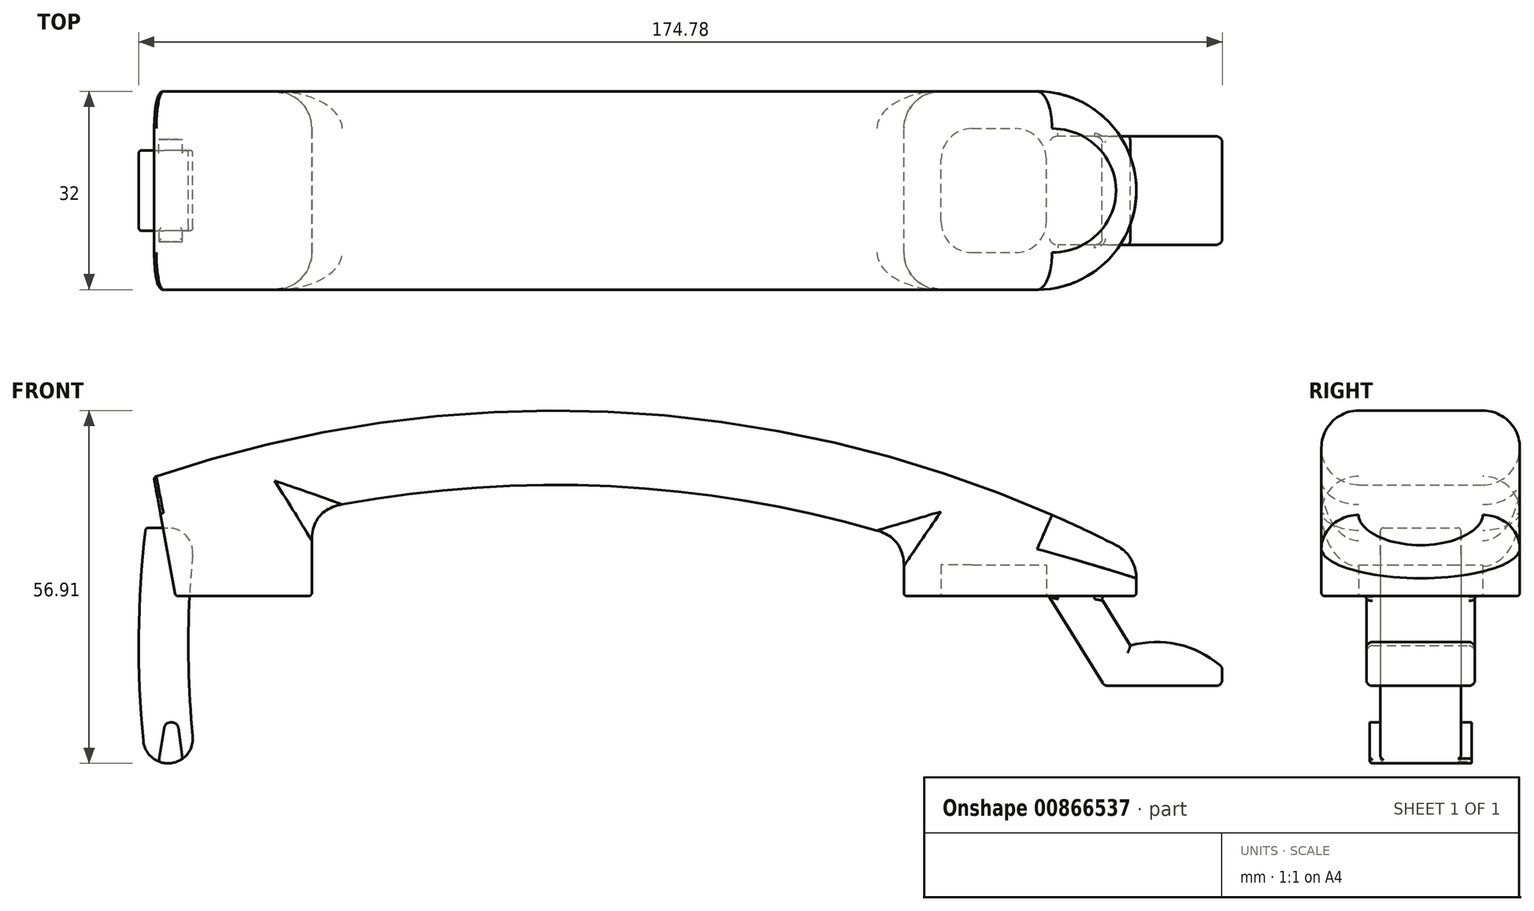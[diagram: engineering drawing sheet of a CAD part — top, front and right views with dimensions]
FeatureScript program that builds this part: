
annotation { "Feature Type Name" : "Feature", "Feature Type Description" : "" }
export const myFeature = defineFeature(function(context is Context, id is Id, definition is map)
    precondition{}
    {
        {
            var Q0;
            Q0=qCreatedBy(makeId("Front.planeOp"),FACE);
            var sketch = newSketch(context, id + "F0", { "sketchPlane" : qUnion([Q0])});
            skLineSegment(sketch, "E0", {"start": v(0, 0) * mm, "end": v(155, 0) * mm, "construction": true});
            skLineSegment(sketch, "E1", {"start": v(155, 0) * mm, "end": v(155, 6.5) * mm});
            skLineSegment(sketch, "E2", {"start": v(0, 0) * mm, "end": v(-3.5, 0) * mm});
            skLineSegment(sketch, "E3", {"start": v(0, 0) * mm, "end": v(-3.5, 19.18) * mm});
            skArc(sketch, "E4", {"start": v(155, 6.5) * mm, "mid": v(77.06, 29.27) * mm, "end": v(-3.5, 19.18) * mm});
            skLineSegment(sketch, "E5", {"start": v(155, 0) * mm, "end": v(117.5, 0) * mm});
            skLineSegment(sketch, "E6", {"start": v(117.5, 0) * mm, "end": v(117.5, 9.25) * mm});
            skArc(sketch, "E7.trimOffspring", {"start": v(117.5, 9.25) * mm, "mid": v(70.04, 17.7) * mm, "end": v(22, 13.8) * mm});
            skLineSegment(sketch, "E8", {"start": v(0, 0) * mm, "end": v(22, 0) * mm});
            skLineSegment(sketch, "E9", {"start": v(22, 0) * mm, "end": v(22, 13.8) * mm});
            skSolve(sketch);
        }
        {
            var Q0;
            Q0 = qSketchRegion(id + "F0", true);
            extrude(context, id + "F1", {"entities" : qUnion([Q0]), "endBound" : BoundingType.SYMMETRIC, "depth" : 32 * mm, "offsetDistance" : 25 * mm});
        }
        {
            var Q0;
            Q0=makeQuery(id+"F1.opExtrude","CAP_EDGE",EDGE,{"disambiguationData":[OSD([sQuery(id+"F0.wireOp",EDGE,"E1")])],"isStart":true});
            var Q1;
            Q1=makeQuery(id+"F1.opExtrude","CAP_EDGE",EDGE,{"disambiguationData":[OSD([sQuery(id+"F0.wireOp",EDGE,"E1")])],"isStart":false});
            fillet(context, id + "F2", {"entities" : qUnion([Q0, Q1]), "radius" : 16 * mm, "tangentPropagation" : true, "allowEdgeOverflow" : false});
        }
        {
            var Q0;
            Q0=makeQuery(id+"F1.opExtrude","CAP_EDGE",EDGE,{"disambiguationData":[OSD([sQuery(id+"F0.wireOp",EDGE,"E4")])],"isStart":false});
            var Q1;
            Q1=makeQuery(id+"F1.opExtrude","CAP_EDGE",EDGE,{"disambiguationData":[OSD([sQuery(id+"F0.wireOp",EDGE,"E7.trimOffspring")])],"isStart":false});
            var Q2;
            Q2=makeQuery(id+"F1.opExtrude","CAP_EDGE",EDGE,{"disambiguationData":[OSD([sQuery(id+"F0.wireOp",EDGE,"E7.trimOffspring")])],"isStart":true});
            var Q3;
            Q3=makeQuery(id+"F1.opExtrude","CAP_EDGE",EDGE,{"disambiguationData":[OSD([sQuery(id+"F0.wireOp",EDGE,"E6")])],"isStart":true});
            var Q4;
            Q4=makeQuery(id+"F1.opExtrude","CAP_EDGE",EDGE,{"disambiguationData":[OSD([sQuery(id+"F0.wireOp",EDGE,"E6")])],"isStart":false});
            var Q5;
            Q5=makeQuery(id+"F1.opExtrude","CAP_EDGE",EDGE,{"disambiguationData":[OSD([sQuery(id+"F0.wireOp",EDGE,"E9")])],"isStart":false});
            var Q6;
            Q6=makeQuery(id+"F1.opExtrude","CAP_EDGE",EDGE,{"disambiguationData":[OSD([sQuery(id+"F0.wireOp",EDGE,"E4")])],"isStart":true});
            var Q7;
            Q7=makeQuery(id+"F1.opExtrude","CAP_EDGE",EDGE,{"disambiguationData":[OSD([sQuery(id+"F0.wireOp",EDGE,"E9")])],"isStart":true});
            fillet(context, id + "F3", {"entities" : qUnion([Q0, Q1, Q2, Q3, Q4, Q5, Q6, Q7]), "radius" : 6 * mm, "tangentPropagation" : true, "allowEdgeOverflow" : false});
        }
        {
            var Q0;
            Q0=makeQuery(id+"F3.opFillet","BLEND_EDGE",EDGE,{"blendedFrom":[makeQuery(id+"F1.opExtrude","CAP_EDGE",EDGE,{"disambiguationData":[OSD([sQuery(id+"F0.wireOp",EDGE,"E6")])],"isStart":false}),makeQuery(id+"F1.opExtrude","CAP_EDGE",EDGE,{"disambiguationData":[OSD([sQuery(id+"F0.wireOp",EDGE,"E7.trimOffspring")])],"isStart":false})],"blendedInto":[]});
            var Q1;
            Q1=makeQuery(id+"F3.opFillet","BLEND_EDGE",EDGE,{"blendedFrom":[makeQuery(id+"F1.opExtrude","CAP_EDGE",EDGE,{"disambiguationData":[OSD([sQuery(id+"F0.wireOp",EDGE,"E7.trimOffspring")])],"isStart":false}),makeQuery(id+"F1.opExtrude","CAP_EDGE",EDGE,{"disambiguationData":[OSD([sQuery(id+"F0.wireOp",EDGE,"E9")])],"isStart":false})],"blendedInto":[]});
            var Q2;
            {var subQ0=sQuery(id+"F0.wireOp",EDGE,"E1");Q2=makeQuery(id+"F3.opFillet","BLEND_EDGE",EDGE,{"blendedFrom":[makeQuery(id+"F2.opFillet","BLEND_EDGE",EDGE,{"blendedFrom":[makeQuery(id+"F1.opExtrude","CAP_EDGE",EDGE,{"disambiguationData":[OSD([subQ0])],"isStart":false}),makeQuery(id+"F1.opExtrude","SWEPT_FACE",FACE,{"disambiguationData":[OSD([sQuery(id+"F0.wireOp",EDGE,"E4")])]})],"blendedInto":[makeQuery(id+"F1.opExtrude","SWEPT_FACE",FACE,{"disambiguationData":[OSD([sQuery(id+"F0.wireOp",EDGE,"E4")])]})]}),makeQuery(id+"F2.opFillet","BLEND_FACE",FACE,{"disambiguationData":[OSD([subQ0])]})],"blendedInto":[makeQuery(id+"F2.opFillet","BLEND_FACE",FACE,{"disambiguationData":[OSD([subQ0])]})]});}
            var Q3;
            {var subQ0=makeQuery(id+"F1.opExtrude","SWEPT_FACE",FACE,{"disambiguationData":[OSD([sQuery(id+"F0.wireOp",EDGE,"E4")])]});Q3=makeQuery(id+"F3.opFillet","BLEND_EDGE",EDGE,{"blendedFrom":[makeQuery(id+"F2.opFillet","BLEND_EDGE",EDGE,{"blendedFrom":[makeQuery(id+"F1.opExtrude","CAP_EDGE",EDGE,{"disambiguationData":[OSD([sQuery(id+"F0.wireOp",EDGE,"E1")])],"isStart":false}),subQ0],"blendedInto":[subQ0]}),subQ0],"blendedInto":[subQ0]});}
            var Q4;
            {var subQ0=sQuery(id+"F0.wireOp",EDGE,"E4");Q4=makeQuery(id+"F3.opFillet","BLEND_EDGE",EDGE,{"blendedFrom":[makeQuery(id+"F2.opFillet","BLEND_EDGE",EDGE,{"blendedFrom":[makeQuery(id+"F1.opExtrude","CAP_EDGE",EDGE,{"disambiguationData":[OSD([sQuery(id+"F0.wireOp",EDGE,"E1")])],"isStart":false}),makeQuery(id+"F1.opExtrude","SWEPT_FACE",FACE,{"disambiguationData":[OSD([subQ0])]})],"blendedInto":[makeQuery(id+"F1.opExtrude","SWEPT_FACE",FACE,{"disambiguationData":[OSD([subQ0])]})]}),makeQuery(id+"F1.opExtrude","CAP_EDGE",EDGE,{"disambiguationData":[OSD([subQ0])],"isStart":false})],"blendedInto":[]});}
            var Q5;
            Q5=makeQuery(id+"F3.opFillet","BLEND_EDGE",EDGE,{"blendedFrom":[makeQuery(id+"F1.opExtrude","CAP_EDGE",EDGE,{"disambiguationData":[OSD([sQuery(id+"F0.wireOp",EDGE,"E7.trimOffspring")])],"isStart":true}),makeQuery(id+"F1.opExtrude","CAP_EDGE",EDGE,{"disambiguationData":[OSD([sQuery(id+"F0.wireOp",EDGE,"E9")])],"isStart":true})],"blendedInto":[]});
            var Q6;
            Q6=makeQuery(id+"F3.opFillet","BLEND_EDGE",EDGE,{"blendedFrom":[makeQuery(id+"F1.opExtrude","CAP_EDGE",EDGE,{"disambiguationData":[OSD([sQuery(id+"F0.wireOp",EDGE,"E6")])],"isStart":true}),makeQuery(id+"F1.opExtrude","CAP_EDGE",EDGE,{"disambiguationData":[OSD([sQuery(id+"F0.wireOp",EDGE,"E7.trimOffspring")])],"isStart":true})],"blendedInto":[]});
            var Q7;
            Q7=makeQuery(id+"F1.opExtrude","SWEPT_EDGE",EDGE,{"disambiguationData":[OSD([sQuery(id+"F0.wireOp",EDGE,"E6"),sQuery(id+"F0.wireOp",EDGE,"E7.trimOffspring")])]});
            var Q8;
            Q8=makeQuery(id+"F1.opExtrude","SWEPT_EDGE",EDGE,{"disambiguationData":[OSD([sQuery(id+"F0.wireOp",EDGE,"E7.trimOffspring"),sQuery(id+"F0.wireOp",EDGE,"E9")])]});
            fillet(context, id + "F4", {"entities" : qUnion([Q0, Q1, Q2, Q3, Q4, Q5, Q6, Q7, Q8]), "radius" : 6 * mm, "rho" : 0.5, "crossSection" : FilletCrossSection.CONIC, "allowEdgeOverflow" : false});
        }
        {
            var Q0;
            Q0=qCreatedBy(makeId("Front.planeOp"),FACE);
            var sketch = newSketch(context, id + "F5", { "sketchPlane" : qUnion([Q0])});
            skLineSegment(sketch, "E10", {"start": v(149.36, 0) * mm, "end": v(140.86, 0) * mm});
            skLineSegment(sketch, "E11", {"start": v(149.86, -14.5) * mm, "end": v(140.86, 0) * mm});
            skLineSegment(sketch, "E12.0", {"start": v(154.06, -8) * mm, "end": v(149.1, 0) * mm});
            skLineSegment(sketch, "E13", {"start": v(149.86, -14.5) * mm, "end": v(168.86, -14.5) * mm});
            skLineSegment(sketch, "E14", {"start": v(168.86, -14.5) * mm, "end": v(168.86, -11.5) * mm});
            skArc(sketch, "E15", {"start": v(168.86, -11.5) * mm, "mid": v(161.9, -7.85) * mm, "end": v(154.06, -8) * mm});
            skPoint(sketch, "E16.start.orphan", {"position": v(157.1, 0) * mm});
            skLineSegment(sketch, "E17", {"start": v(155.1, 0) * mm, "end": v(149.1, 0) * mm});
            skSolve(sketch);
        }
        {
            var Q0;
            {var subQ1=sQuery(id+"F5.wireOp",EDGE,"E11");Q0=makeQuery(id+"F5.imprint","IMPRINT",FACE,{"disambiguationData":[TD([[makeQuery(id+"F5.imprint","IMPRINT",EDGE,{"derivedFrom":subQ1}),-1.0]])]});}
            extrude(context, id + "F6", {"entities" : qUnion([Q0]), "operationType" : NewBodyOperationType.ADD, "endBound" : BoundingType.SYMMETRIC, "depth" : 17.5 * mm, "offsetDistance" : 25 * mm});
        }
        {
            var Q0;
            Q0=makeQuery(id+"F6.opExtrude","CAP_EDGE",EDGE,{"disambiguationData":[OSD([sQuery(id+"F5.wireOp",EDGE,"E12.0")])],"isStart":false});
            var Q1;
            Q1=makeQuery(id+"F6.opExtrude","CAP_EDGE",EDGE,{"disambiguationData":[OSD([sQuery(id+"F5.wireOp",EDGE,"E15")])],"isStart":false});
            var Q2;
            Q2=makeQuery(id+"F6.opExtrude","CAP_EDGE",EDGE,{"disambiguationData":[OSD([sQuery(id+"F5.wireOp",EDGE,"E15")])],"isStart":true});
            var Q3;
            Q3=makeQuery(id+"F6.opExtrude","CAP_EDGE",EDGE,{"disambiguationData":[OSD([sQuery(id+"F5.wireOp",EDGE,"E12.0")])],"isStart":true});
            var Q4;
            Q4=makeQuery(id+"F6.opExtrude","SWEPT_EDGE",EDGE,{"disambiguationData":[OSD([sQuery(id+"F5.wireOp",EDGE,"E14"),sQuery(id+"F5.wireOp",EDGE,"E15")])]});
            var Q5;
            Q5=makeQuery(id+"F6.opExtrude","CAP_EDGE",EDGE,{"disambiguationData":[OSD([sQuery(id+"F5.wireOp",EDGE,"E11")])],"isStart":false});
            var Q6;
            Q6=makeQuery(id+"F6.opExtrude","CAP_EDGE",EDGE,{"disambiguationData":[OSD([sQuery(id+"F5.wireOp",EDGE,"E13")])],"isStart":false});
            var Q7;
            Q7=makeQuery(id+"F6.opExtrude","SWEPT_EDGE",EDGE,{"disambiguationData":[OSD([sQuery(id+"F5.wireOp",EDGE,"E11"),sQuery(id+"F5.wireOp",EDGE,"E13")])]});
            var Q8;
            Q8=makeQuery(id+"F6.opExtrude","CAP_EDGE",EDGE,{"disambiguationData":[OSD([sQuery(id+"F5.wireOp",EDGE,"E11")])],"isStart":true});
            var Q9;
            Q9=makeQuery(id+"F6.opExtrude","CAP_EDGE",EDGE,{"disambiguationData":[OSD([sQuery(id+"F5.wireOp",EDGE,"E13")])],"isStart":true});
            var Q10;
            Q10=makeQuery(id+"F6.opExtrude","SWEPT_FACE",FACE,{"disambiguationData":[OSD([sQuery(id+"F5.wireOp",EDGE,"E14")])]});
            fillet(context, id + "F7", {"entities" : qUnion([Q0, Q1, Q2, Q3, Q4, Q5, Q6, Q7, Q8, Q9, Q10]), "radius" : 1 * mm, "tangentPropagation" : true, "allowEdgeOverflow" : false});
        }
        {
            var Q0;
            Q0=qCreatedBy(makeId("Front.planeOp"),FACE);
            var sketch = newSketch(context, id + "F8", { "sketchPlane" : qUnion([Q0])});
            skArc(sketch, "E18", {"start": v(-4.8, 11) * mm, "mid": v(-5.92, -8) * mm, "end": v(-4.79, -27) * mm});
            skArc(sketch, "E19.0", {"start": v(3.26, 11) * mm, "mid": v(2.08, -8) * mm, "end": v(3.27, -27) * mm});
            skLineSegment(sketch, "E20", {"start": v(0, -27) * mm, "end": v(3.27, -27) * mm});
            skLineSegment(sketch, "E21", {"start": v(3.27, -27) * mm, "end": v(-4.79, -27) * mm});
            skLineSegment(sketch, "E22", {"start": v(0, 11) * mm, "end": v(-4.8, 11) * mm});
            skLineSegment(sketch, "E23", {"start": v(0, 11) * mm, "end": v(3.26, 11) * mm});
            skSolve(sketch);
        }
        {
            var Q0;
            {var subQ1=sQuery(id+"F8.wireOp",EDGE,"E18");Q0=makeQuery(id+"F8.imprint","IMPRINT",FACE,{"disambiguationData":[TD([[makeQuery(id+"F8.imprint","IMPRINT",EDGE,{"derivedFrom":subQ1}),1.0]])]});}
            extrude(context, id + "F9", {"entities" : qUnion([Q0]), "endBound" : BoundingType.SYMMETRIC, "depth" : 13 * mm, "offsetDistance" : 25 * mm});
        }
        {
            var Q0;
            Q0=qCreatedBy(makeId("Front.planeOp"),FACE);
            var sketch = newSketch(context, id + "F10", { "sketchPlane" : qUnion([Q0])});
            skLineSegment(sketch, "E24", {"start": v(-0.76, -27) * mm, "end": v(1.24, -27) * mm});
            skLineSegment(sketch, "E25", {"start": v(-0.76, -27) * mm, "end": v(-2.76, -27) * mm});
            skLineSegment(sketch, "E26", {"start": v(-0.66, -20.4) * mm, "end": v(-0.53, -20.4) * mm});
            skLineSegment(sketch, "E27", {"start": v(-0.66, -20.4) * mm, "end": v(-0.81, -20.4) * mm});
            skLineSegment(sketch, "E28", {"start": v(-1.8, -21.24) * mm, "end": v(-2.76, -27) * mm});
            skLineSegment(sketch, "E29", {"start": v(0.46, -21.27) * mm, "end": v(1.24, -27) * mm});
            skPoint(sketch, "E30.visualSharp", {"position": v(-1.66, -20.4) * mm});
            skArc(sketch, "E30.filletArc", {"start": v(-0.81, -20.4) * mm, "mid": v(-1.46, -20.64) * mm, "end": v(-1.8, -21.24) * mm});
            skPoint(sketch, "E31.visualSharp", {"position": v(0.34, -20.4) * mm});
            skArc(sketch, "E31.filletArc", {"start": v(0.46, -21.27) * mm, "mid": v(0.13, -20.65) * mm, "end": v(-0.53, -20.4) * mm});
            skSolve(sketch);
        }
        {
            var Q0;
            Q0 = qSketchRegion(id + "F10", true);
            var Q1;
            Q1 = qConstructionFilter(qBodyType(qCreatedBy(id + "F10" ,EDGE), BodyType.WIRE), ConstructionObject.NO);
            extrude(context, id + "F11", {"entities" : qUnion([Q0]), "operationType" : NewBodyOperationType.ADD, "surfaceEntities" : qUnion([Q1]), "endBound" : BoundingType.SYMMETRIC, "depth" : 16.5 * mm, "offsetDistance" : 25 * mm});
        }
        {
            var Q0;
            Q0=makeQuery(id+"F9.opExtrude","SWEPT_EDGE",EDGE,{"disambiguationData":[OSD([sQuery(id+"F8.wireOp",EDGE,"E18"),sQuery(id+"F8.wireOp",EDGE,"E21")])]});
            var Q1;
            Q1=makeQuery(id+"F9.opExtrude","SWEPT_EDGE",EDGE,{"disambiguationData":[OSD([sQuery(id+"F8.wireOp",EDGE,"E19.0"),sQuery(id+"F8.wireOp",EDGE,"E21")])]});
            fillet(context, id + "F12", {"entities" : qUnion([Q0, Q1]), "radius" : 4 * mm, "tangentPropagation" : true, "allowEdgeOverflow" : false});
        }
        {
            var Q0;
            Q0=makeQuery(id+"F1.opExtrude","SWEPT_EDGE",EDGE,{"disambiguationData":[OSD([sQuery(id+"F0.wireOp",EDGE,"E3"),sQuery(id+"F0.wireOp",EDGE,"E4")])]});
            var Q1;
            Q1=makeQuery(id+"F1.opExtrude","CAP_EDGE",EDGE,{"disambiguationData":[OSD([sQuery(id+"F0.wireOp",EDGE,"E8")])],"isStart":true});
            var Q2;
            Q2=makeQuery(id+"F1.opExtrude","SWEPT_EDGE",EDGE,{"disambiguationData":[OSD([sQuery(id+"F0.wireOp",EDGE,"E3"),sQuery(id+"F0.wireOp",EDGE,"E8")])]});
            var Q3;
            Q3=makeQuery(id+"F12.opFillet","BLEND_EDGE",EDGE,{"blendedFrom":[makeQuery(id+"F9.opExtrude","SWEPT_EDGE",EDGE,{"disambiguationData":[OSD([sQuery(id+"F8.wireOp",EDGE,"E18"),sQuery(id+"F8.wireOp",EDGE,"E21")])]}),makeQuery(id+"F11.opExtrude","CAP_FACE",FACE,{"disambiguationData":[OSD([sQuery(id+"F10.wireOp",EDGE,"E24"),sQuery(id+"F10.wireOp",EDGE,"E25"),sQuery(id+"F10.wireOp",EDGE,"E26"),sQuery(id+"F10.wireOp",EDGE,"E27"),sQuery(id+"F10.wireOp",EDGE,"E28"),sQuery(id+"F10.wireOp",EDGE,"E29"),sQuery(id+"F10.wireOp",EDGE,"E30.filletArc"),sQuery(id+"F10.wireOp",EDGE,"E31.filletArc")])],"isStart":false})],"blendedInto":[makeQuery(id+"F11.opExtrude","CAP_FACE",FACE,{"disambiguationData":[OSD([sQuery(id+"F10.wireOp",EDGE,"E24"),sQuery(id+"F10.wireOp",EDGE,"E25"),sQuery(id+"F10.wireOp",EDGE,"E26"),sQuery(id+"F10.wireOp",EDGE,"E27"),sQuery(id+"F10.wireOp",EDGE,"E28"),sQuery(id+"F10.wireOp",EDGE,"E29"),sQuery(id+"F10.wireOp",EDGE,"E30.filletArc"),sQuery(id+"F10.wireOp",EDGE,"E31.filletArc")])],"isStart":false})]});
            var Q4;
            {var subQ0=sQuery(id+"F8.wireOp",EDGE,"E21");var subQ1=sQuery(id+"F8.wireOp",EDGE,"E18");Q4=makeQuery(id+"F12.opFillet","BLEND_EDGE",EDGE,{"blendedFrom":[makeQuery(id+"F9.opExtrude","SWEPT_EDGE",EDGE,{"disambiguationData":[OSD([subQ1,subQ0])]}),makeQuery(id+"F9.opExtrude","CAP_FACE",FACE,{"disambiguationData":[OSD([subQ1,sQuery(id+"F8.wireOp",EDGE,"E19.0"),subQ0,sQuery(id+"F8.wireOp",EDGE,"E22"),sQuery(id+"F8.wireOp",EDGE,"E23")])],"isStart":false})],"blendedInto":[makeQuery(id+"F9.opExtrude","CAP_FACE",FACE,{"disambiguationData":[OSD([subQ1,sQuery(id+"F8.wireOp",EDGE,"E19.0"),subQ0,sQuery(id+"F8.wireOp",EDGE,"E22"),sQuery(id+"F8.wireOp",EDGE,"E23")])],"isStart":false})]});}
            var Q5;
            {var subQ0=sQuery(id+"F8.wireOp",EDGE,"E21");var subQ1=sQuery(id+"F8.wireOp",EDGE,"E19.0");Q5=makeQuery(id+"F12.opFillet","BLEND_EDGE",EDGE,{"blendedFrom":[makeQuery(id+"F9.opExtrude","SWEPT_EDGE",EDGE,{"disambiguationData":[OSD([subQ1,subQ0])]}),makeQuery(id+"F9.opExtrude","CAP_FACE",FACE,{"disambiguationData":[OSD([sQuery(id+"F8.wireOp",EDGE,"E18"),subQ1,subQ0,sQuery(id+"F8.wireOp",EDGE,"E22"),sQuery(id+"F8.wireOp",EDGE,"E23")])],"isStart":false})],"blendedInto":[makeQuery(id+"F9.opExtrude","CAP_FACE",FACE,{"disambiguationData":[OSD([sQuery(id+"F8.wireOp",EDGE,"E18"),subQ1,subQ0,sQuery(id+"F8.wireOp",EDGE,"E22"),sQuery(id+"F8.wireOp",EDGE,"E23")])],"isStart":false})]});}
            var Q6;
            {var subQ1=sQuery(id+"F10.wireOp",EDGE,"E28");var subQ4=sQuery(id+"F8.wireOp",EDGE,"E21");var subQ5=sQuery(id+"F8.wireOp",EDGE,"E18");Q6=makeQuery(id+"F12.opFillet","BLEND_EDGE",EDGE,{"blendedFrom":[makeQuery(id+"F9.opExtrude","SWEPT_EDGE",EDGE,{"disambiguationData":[OSD([subQ5,subQ4])]}),makeQuery(id+"F11.boolean.opBoolean","SPLIT",FACE,{"disambiguationData":[TD([makeQuery(id+"F9.opExtrude","CAP_FACE",FACE,{"disambiguationData":[OSD([subQ5,sQuery(id+"F8.wireOp",EDGE,"E19.0"),subQ4,sQuery(id+"F8.wireOp",EDGE,"E22"),sQuery(id+"F8.wireOp",EDGE,"E23")])],"isStart":false})])],"derivedFrom":makeQuery(id+"F11.opExtrude","SWEPT_FACE",FACE,{"disambiguationData":[OSD([subQ1])]})})],"blendedInto":[makeQuery(id+"F11.boolean.opBoolean","SPLIT",FACE,{"disambiguationData":[TD([makeQuery(id+"F9.opExtrude","CAP_FACE",FACE,{"disambiguationData":[OSD([subQ5,sQuery(id+"F8.wireOp",EDGE,"E19.0"),subQ4,sQuery(id+"F8.wireOp",EDGE,"E22"),sQuery(id+"F8.wireOp",EDGE,"E23")])],"isStart":false})])],"derivedFrom":makeQuery(id+"F11.opExtrude","SWEPT_FACE",FACE,{"disambiguationData":[OSD([subQ1])]})})]});}
            var Q7;
            {var subQ1=sQuery(id+"F10.wireOp",EDGE,"E29");var subQ4=sQuery(id+"F8.wireOp",EDGE,"E21");var subQ5=sQuery(id+"F8.wireOp",EDGE,"E19.0");Q7=makeQuery(id+"F12.opFillet","BLEND_EDGE",EDGE,{"blendedFrom":[makeQuery(id+"F9.opExtrude","SWEPT_EDGE",EDGE,{"disambiguationData":[OSD([subQ5,subQ4])]}),makeQuery(id+"F11.boolean.opBoolean","SPLIT",FACE,{"disambiguationData":[TD([makeQuery(id+"F9.opExtrude","CAP_FACE",FACE,{"disambiguationData":[OSD([sQuery(id+"F8.wireOp",EDGE,"E18"),subQ5,subQ4,sQuery(id+"F8.wireOp",EDGE,"E22"),sQuery(id+"F8.wireOp",EDGE,"E23")])],"isStart":false})])],"derivedFrom":makeQuery(id+"F11.opExtrude","SWEPT_FACE",FACE,{"disambiguationData":[OSD([subQ1])]})})],"blendedInto":[makeQuery(id+"F11.boolean.opBoolean","SPLIT",FACE,{"disambiguationData":[TD([makeQuery(id+"F9.opExtrude","CAP_FACE",FACE,{"disambiguationData":[OSD([sQuery(id+"F8.wireOp",EDGE,"E18"),subQ5,subQ4,sQuery(id+"F8.wireOp",EDGE,"E22"),sQuery(id+"F8.wireOp",EDGE,"E23")])],"isStart":false})])],"derivedFrom":makeQuery(id+"F11.opExtrude","SWEPT_FACE",FACE,{"disambiguationData":[OSD([subQ1])]})})]});}
            var Q8;
            Q8=makeQuery(id+"F1.opExtrude","SWEPT_FACE",FACE,{"disambiguationData":[OSD([sQuery(id+"F0.wireOp",EDGE,"E5")])]});
            var Q9;
            Q9=makeQuery(id+"F9.opExtrude","SWEPT_EDGE",EDGE,{"disambiguationData":[OSD([sQuery(id+"F8.wireOp",EDGE,"E18"),sQuery(id+"F8.wireOp",EDGE,"E22")])]});
            var Q10;
            Q10=makeQuery(id+"F9.opExtrude","CAP_EDGE",EDGE,{"disambiguationData":[OSD([sQuery(id+"F8.wireOp",EDGE,"E18")])],"isStart":true});
            var Q11;
            Q11=makeQuery(id+"F9.opExtrude","CAP_EDGE",EDGE,{"disambiguationData":[OSD([sQuery(id+"F8.wireOp",EDGE,"E19.0")])],"isStart":true});
            fillet(context, id + "F13", {"entities" : qUnion([Q0, Q1, Q2, Q3, Q4, Q5, Q6, Q7, Q8, Q9, Q10, Q11]), "radius" : 0.5 * mm, "tangentPropagation" : true, "allowEdgeOverflow" : false});
        }
        {
            var Q0;
            Q0=makeQuery(id+"F1.opExtrude","SWEPT_FACE",FACE,{"disambiguationData":[OSD([sQuery(id+"F0.wireOp",EDGE,"E5")])]});
            var sketch = newSketch(context, id + "F14", { "sketchPlane" : qUnion([Q0])});
            skLineSegment(sketch, "E32.bottom", {"start": v(123.5, 10) * mm, "end": v(123.5, 10) * mm});
            skLineSegment(sketch, "E32.top", {"start": v(123.5, -10) * mm, "end": v(123.5, -10) * mm});
            skLineSegment(sketch, "E33.bottom", {"start": v(128.5, 10) * mm, "end": v(135.5, 10) * mm});
            skLineSegment(sketch, "E33.top", {"start": v(128.5, -10) * mm, "end": v(135.5, -10) * mm});
            skLineSegment(sketch, "E33.left", {"start": v(123.5, 5) * mm, "end": v(123.5, -5) * mm});
            skLineSegment(sketch, "E33.right", {"start": v(140.5, 5) * mm, "end": v(140.5, -5) * mm});
            skPoint(sketch, "E34.visualSharp", {"position": v(123.5, 10) * mm});
            skArc(sketch, "E34.filletArc", {"start": v(128.5, 10) * mm, "mid": v(124.96, 8.54) * mm, "end": v(123.5, 5) * mm});
            skPoint(sketch, "E35.visualSharp", {"position": v(140.5, 10) * mm});
            skArc(sketch, "E35.filletArc", {"start": v(140.5, 5) * mm, "mid": v(139.04, 8.54) * mm, "end": v(135.5, 10) * mm});
            skPoint(sketch, "E36.visualSharp", {"position": v(123.5, -10) * mm});
            skArc(sketch, "E36.filletArc", {"start": v(123.5, -5) * mm, "mid": v(124.96, -8.54) * mm, "end": v(128.5, -10) * mm});
            skPoint(sketch, "E37.visualSharp", {"position": v(140.5, -10) * mm});
            skArc(sketch, "E37.filletArc", {"start": v(135.5, -10) * mm, "mid": v(139.04, -8.54) * mm, "end": v(140.5, -5) * mm});
            skSolve(sketch);
        }
        {
            var Q0;
            Q0 = qSketchRegion(id + "F14", true);
            extrude(context, id + "F15", {"entities" : qUnion([Q0]), "operationType" : NewBodyOperationType.REMOVE, "oppositeDirection" : true, "depth" : 5 * mm, "offsetDistance" : 25 * mm});
        }
    });
